FCSTD DOCUMENT  (FreeCAD 1.0R39109 (Git))
Label: Master Document
License: All rights reserved
LicenseURL: http://en.wikipedia.org/wiki/All_rights_reserved
objects: Spreadsheet::Sheet×1

FEATURE [Spreadsheet::Sheet] Spreadsheet  label="Monitor Chassis Parameters"
  cells = A1='Parameter Name; B1='Value; C1='Notes; A2='PiFilterHolderLensOuterDiameter; B2(PiFilterHolderLensOuterDiameter)=30.1; A3='PiFilterHolderLensLipDepth; B3(PiFilterHolderLensLipDepth)=7; A4='PiFilterHolderFilterSide; B4(PiFilterHolderFilterSide)=25.5; C4='1 inch; A5='PiFilterHolderFilterThickness; B5(PiFilterHolderFilterThickness)=1.5; C5='If desired, can be a  tenth of a mm or so thicker than the filter to allow for easier insertion; A6='PiFilterHolderBodyWallThickness; B6(PiFilterHolderBodyWallThickness)=2.5; A7='PiFilterHolderTensionCutWidth; B7(PiFilterHolderTensionCutWidth)=2; A8='PiFilterInnerRadiusCutIn; B8(PiFilterInnerRadiusCutIn)=5; C8='Accounts for the fact that the actual lens (as well as a 1 inch filter square) is quite a bit smaller than the outside of the lens body
